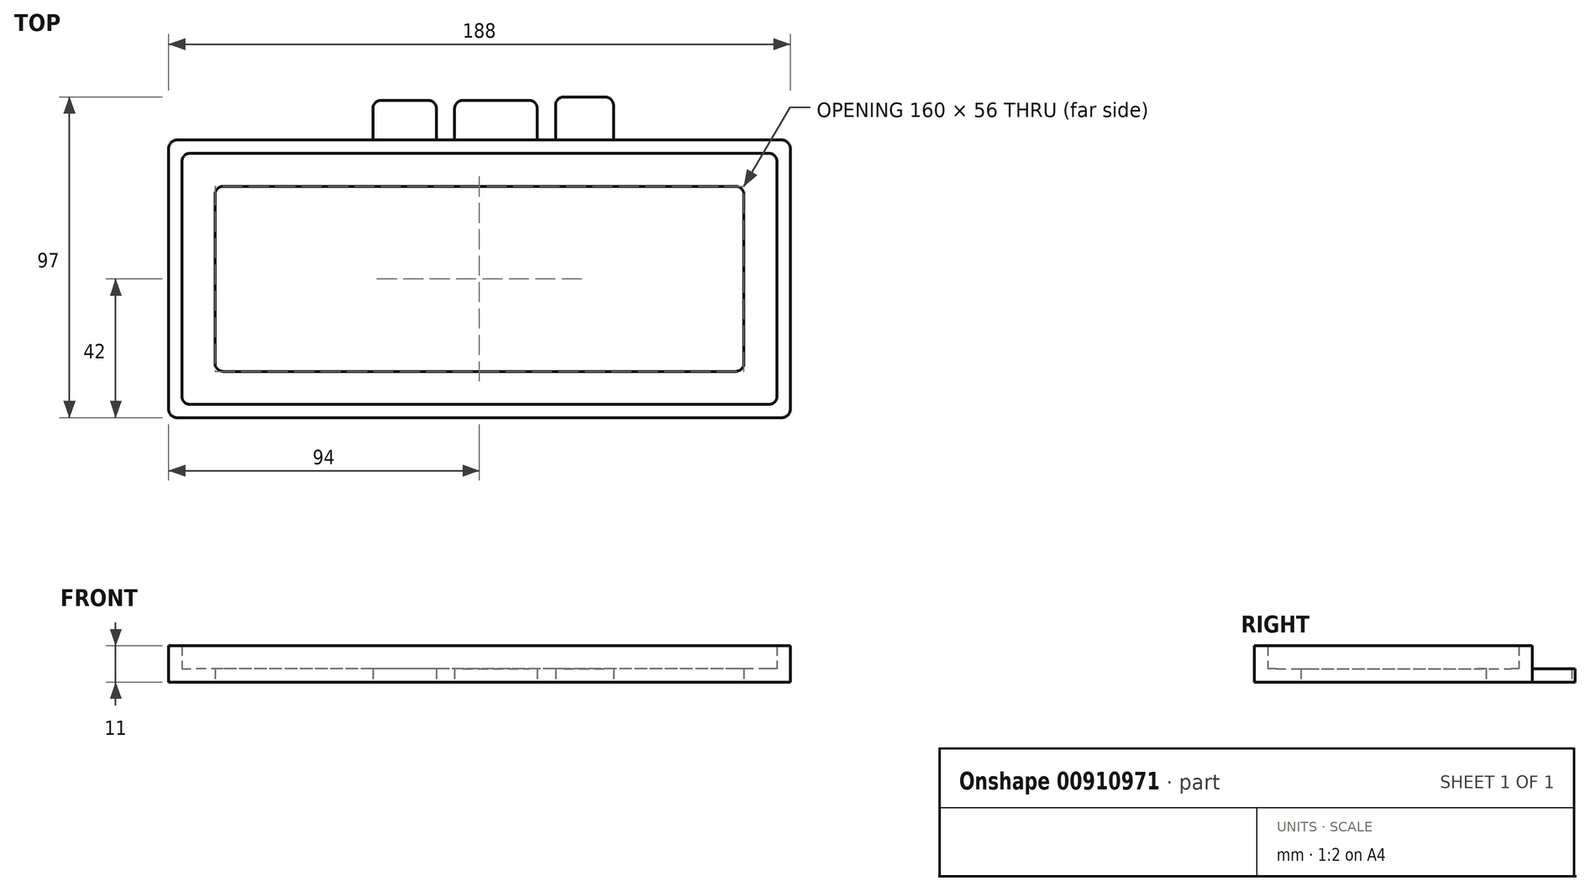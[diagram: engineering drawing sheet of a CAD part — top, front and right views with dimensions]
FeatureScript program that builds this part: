
annotation { "Feature Type Name" : "Feature", "Feature Type Description" : "" }
export const myFeature = defineFeature(function(context is Context, id is Id, definition is map)
    precondition{}
    {
        {
            var Q0;
            Q0=qCreatedBy(makeId("Top.planeOp"),FACE);
            var sketch = newSketch(context, id + "F0", { "sketchPlane" : qUnion([Q0])});
            skLineSegment(sketch, "E0.bottom", {"start": v(87.5, 0) * mm, "end": v(-87.5, 0) * mm});
            skLineSegment(sketch, "E0.top", {"start": v(87.5, 76) * mm, "end": v(-87.5, 76) * mm});
            skLineSegment(sketch, "E0.left", {"start": v(90, 2.5) * mm, "end": v(90, 73.5) * mm});
            skLineSegment(sketch, "E0.right", {"start": v(-90, 2.5) * mm, "end": v(-90, 73.5) * mm});
            skLineSegment(sketch, "E1.0", {"start": v(101.5, 80) * mm, "end": v(-74.5, 80) * mm});
            skLineSegment(sketch, "E2.0", {"start": v(-94, 0) * mm, "end": v(-94, 76) * mm});
            skLineSegment(sketch, "E3.0", {"start": v(88, -4) * mm, "end": v(-88, -4) * mm});
            skLineSegment(sketch, "E4.0", {"start": v(94, 0) * mm, "end": v(94, 76) * mm});
            skLineSegment(sketch, "E5", {"start": v(-74.5, 80) * mm, "end": v(-91.5, 80) * mm});
            skLineSegment(sketch, "E6", {"start": v(-94, 76) * mm, "end": v(-94, 77.5) * mm});
            skLineSegment(sketch, "E7", {"start": v(-94, -1.5) * mm, "end": v(-94, 0) * mm});
            skLineSegment(sketch, "E8", {"start": v(-88, -4) * mm, "end": v(-91.5, -4) * mm});
            skLineSegment(sketch, "E9", {"start": v(91.5, 80) * mm, "end": v(101.5, 80) * mm});
            skLineSegment(sketch, "E10", {"start": v(94, 77.5) * mm, "end": v(94, 76) * mm});
            skLineSegment(sketch, "E11", {"start": v(88, -4) * mm, "end": v(91.5, -4) * mm});
            skLineSegment(sketch, "E12", {"start": v(94, -1.5) * mm, "end": v(94, 0) * mm});
            skLineSegment(sketch, "E13", {"start": v(-7.5, 80) * mm, "end": v(-7.5, 89.5) * mm});
            skLineSegment(sketch, "E14", {"start": v(-5, 92) * mm, "end": v(15, 92) * mm});
            skLineSegment(sketch, "E15", {"start": v(17.5, 89.5) * mm, "end": v(17.5, 80) * mm});
            skLineSegment(sketch, "E16", {"start": v(5, 92) * mm, "end": v(5, 80) * mm, "construction": true});
            skLineSegment(sketch, "E17", {"start": v(5, 80) * mm, "end": v(5, 76) * mm, "construction": true});
            skLineSegment(sketch, "E18", {"start": v(-13, 80) * mm, "end": v(-13, 89.5) * mm});
            skLineSegment(sketch, "E19", {"start": v(-15.5, 92) * mm, "end": v(-29.75, 92) * mm});
            skLineSegment(sketch, "E20", {"start": v(-32.25, 89.5) * mm, "end": v(-32.25, 80) * mm});
            skLineSegment(sketch, "E21", {"start": v(23, 80) * mm, "end": v(23, 90.5) * mm});
            skLineSegment(sketch, "E22", {"start": v(25.5, 93) * mm, "end": v(38.05, 93) * mm});
            skLineSegment(sketch, "E23", {"start": v(40.55, 90.5) * mm, "end": v(40.55, 80) * mm});
            skPoint(sketch, "E24.visualSharp", {"position": v(17.5, 92) * mm});
            skArc(sketch, "E24.filletArc", {"start": v(17.5, 89.5) * mm, "mid": v(16.77, 91.27) * mm, "end": v(15, 92) * mm});
            skPoint(sketch, "E25.visualSharp", {"position": v(-7.5, 92) * mm});
            skArc(sketch, "E25.filletArc", {"start": v(-5, 92) * mm, "mid": v(-6.77, 91.27) * mm, "end": v(-7.5, 89.5) * mm});
            skPoint(sketch, "E26.visualSharp", {"position": v(-13, 92) * mm});
            skArc(sketch, "E26.filletArc", {"start": v(-13, 89.5) * mm, "mid": v(-13.73, 91.27) * mm, "end": v(-15.5, 92) * mm});
            skPoint(sketch, "E27.visualSharp", {"position": v(23, 93) * mm});
            skArc(sketch, "E27.filletArc", {"start": v(25.5, 93) * mm, "mid": v(23.73, 92.27) * mm, "end": v(23, 90.5) * mm});
            skPoint(sketch, "E28.visualSharp", {"position": v(-32.25, 92) * mm});
            skArc(sketch, "E28.filletArc", {"start": v(-29.75, 92) * mm, "mid": v(-31.52, 91.27) * mm, "end": v(-32.25, 89.5) * mm});
            skPoint(sketch, "E29.visualSharp", {"position": v(40.55, 93) * mm});
            skArc(sketch, "E29.filletArc", {"start": v(40.55, 90.5) * mm, "mid": v(39.82, 92.27) * mm, "end": v(38.05, 93) * mm});
            skPoint(sketch, "E30.visualSharp", {"position": v(-90, 76) * mm});
            skArc(sketch, "E30.filletArc", {"start": v(-87.5, 76) * mm, "mid": v(-89.27, 75.27) * mm, "end": v(-90, 73.5) * mm});
            skPoint(sketch, "E31.visualSharp", {"position": v(-94, 80) * mm});
            skArc(sketch, "E31.filletArc", {"start": v(-91.5, 80) * mm, "mid": v(-93.27, 79.27) * mm, "end": v(-94, 77.5) * mm});
            skPoint(sketch, "E32.visualSharp", {"position": v(-90, 0) * mm});
            skArc(sketch, "E32.filletArc", {"start": v(-90, 2.5) * mm, "mid": v(-89.27, 0.73) * mm, "end": v(-87.5, 0) * mm});
            skPoint(sketch, "E33.visualSharp", {"position": v(-94, -4) * mm});
            skArc(sketch, "E33.filletArc", {"start": v(-94, -1.5) * mm, "mid": v(-93.27, -3.27) * mm, "end": v(-91.5, -4) * mm});
            skPoint(sketch, "E34.visualSharp", {"position": v(94, -4) * mm});
            skArc(sketch, "E34.filletArc", {"start": v(91.5, -4) * mm, "mid": v(93.27, -3.27) * mm, "end": v(94, -1.5) * mm});
            skPoint(sketch, "E35.visualSharp", {"position": v(90, 0) * mm});
            skArc(sketch, "E35.filletArc", {"start": v(87.5, 0) * mm, "mid": v(89.27, 0.73) * mm, "end": v(90, 2.5) * mm});
            skPoint(sketch, "E36.visualSharp", {"position": v(90, 76) * mm});
            skArc(sketch, "E36.filletArc", {"start": v(90, 73.5) * mm, "mid": v(89.27, 75.27) * mm, "end": v(87.5, 76) * mm});
            skPoint(sketch, "E37.visualSharp", {"position": v(94, 80) * mm});
            skArc(sketch, "E37.filletArc", {"start": v(94, 77.5) * mm, "mid": v(93.27, 79.27) * mm, "end": v(91.5, 80) * mm});
            skLineSegment(sketch, "E38.0", {"start": v(77.5, 66) * mm, "end": v(-77.5, 66) * mm});
            skLineSegment(sketch, "E39.0", {"start": v(80, 12.5) * mm, "end": v(80, 63.5) * mm});
            skLineSegment(sketch, "E40.0", {"start": v(77.5, 10) * mm, "end": v(-77.5, 10) * mm});
            skLineSegment(sketch, "E41.0", {"start": v(-80, 12.5) * mm, "end": v(-80, 63.5) * mm});
            skPoint(sketch, "E42.visualSharp", {"position": v(-80, 66) * mm});
            skArc(sketch, "E42.filletArc", {"start": v(-77.5, 66) * mm, "mid": v(-79.27, 65.27) * mm, "end": v(-80, 63.5) * mm});
            skPoint(sketch, "E43.visualSharp", {"position": v(-80, 10) * mm});
            skArc(sketch, "E43.filletArc", {"start": v(-80, 12.5) * mm, "mid": v(-79.27, 10.73) * mm, "end": v(-77.5, 10) * mm});
            skPoint(sketch, "E44.visualSharp", {"position": v(80, 66) * mm});
            skArc(sketch, "E44.filletArc", {"start": v(80, 63.5) * mm, "mid": v(79.27, 65.27) * mm, "end": v(77.5, 66) * mm});
            skPoint(sketch, "E45.visualSharp", {"position": v(80, 10) * mm});
            skArc(sketch, "E45.filletArc", {"start": v(77.5, 10) * mm, "mid": v(79.27, 10.73) * mm, "end": v(80, 12.5) * mm});
            skSolve(sketch);
        }
        {
            var Q0;
            Q0=makeQuery(id+"F0.imprint","IMPRINT",FACE,{"disambiguationData":[TD([[makeQuery(id+"F0.imprint","IMPRINT",EDGE,{"derivedFrom":sQuery(id+"F0.wireOp",EDGE,"E0.bottom")}),1.0]])]});
            extrude(context, id + "F1", {"entities" : qUnion([Q0]), "depth" : 11 * mm, "offsetDistance" : 25 * mm});
        }
        {
            var Q0;
            Q0=makeQuery(id+"F0.imprint","IMPRINT",FACE,{"disambiguationData":[TD([[makeQuery(id+"F0.imprint","IMPRINT",EDGE,{"derivedFrom":sQuery(id+"F0.wireOp",EDGE,"E0.bottom")}),-1.0]])]});
            var Q1;
            {var subQ1=sQuery(id+"F0.wireOp",EDGE,"E18");Q1=makeQuery(id+"F0.imprint","IMPRINT",FACE,{"disambiguationData":[TD([[makeQuery(id+"F0.imprint","IMPRINT",EDGE,{"derivedFrom":subQ1}),1.0]])]});}
            var Q2;
            {var subQ1=sQuery(id+"F0.wireOp",EDGE,"E13");Q2=makeQuery(id+"F0.imprint","IMPRINT",FACE,{"disambiguationData":[TD([[makeQuery(id+"F0.imprint","IMPRINT",EDGE,{"derivedFrom":subQ1}),-1.0]])]});}
            var Q3;
            {var subQ0=sQuery(id+"F0.wireOp",EDGE,"E21");Q3=makeQuery(id+"F0.imprint","IMPRINT",FACE,{"disambiguationData":[TD([[makeQuery(id+"F0.imprint","IMPRINT",EDGE,{"derivedFrom":subQ0}),-1.0]])]});}
            extrude(context, id + "F2", {"entities" : qUnion([Q0, Q1, Q2, Q3]), "operationType" : NewBodyOperationType.ADD, "depth" : 4 * mm, "offsetDistance" : 25 * mm});
        }
    });
